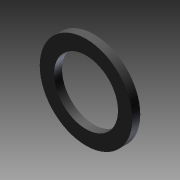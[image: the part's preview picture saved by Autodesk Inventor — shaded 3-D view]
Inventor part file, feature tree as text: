
AUTODESK INVENTOR PART (.ipt)
format: ipt  version: 2011 SP1 (Build 150282100, 282)  size: 80,896 bytes
history: native  units: in
note: dims shown in document units (in); Inventor stores cm internally (conversion verified against a paired STEP export)
features: other x14, revolve x1, sketch x1
ambient origin geometry x8: Origin, YZ Plane, XZ Plane, XY Plane, X Axis, Y Axis, Z Axis, Center Point
bodies: Solid1 (feature_tree)
feature tree (16):
  revolve  "Revolution1"  [1 undecoded]
  other  "o_ring_XY"
  other  "o_ring_YZ"
  other  "o_ring_ZX"
  other  "o_ring_X"
  other  "o_ring_Y"
  other  "o_ring_Z"
  other  "o_ring_Center"
  other  "o_ring_new_XY"
  other  "o_ring_new_YZ"
  other  "o_ring_new_ZX"
  other  "o_ring_new_X"
  other  "o_ring_new_Y"
  other  "o_ring_new_Z"
  other  "o_ring_new_Center"
  sketch  "Sketch_1"  dims[d0=360.0deg]
note: 1 required parameter value undecoded (feature->parameter linkage not recoverable at this tier; creation-order binding heuristic only, values carry confidence <= 0.55)
